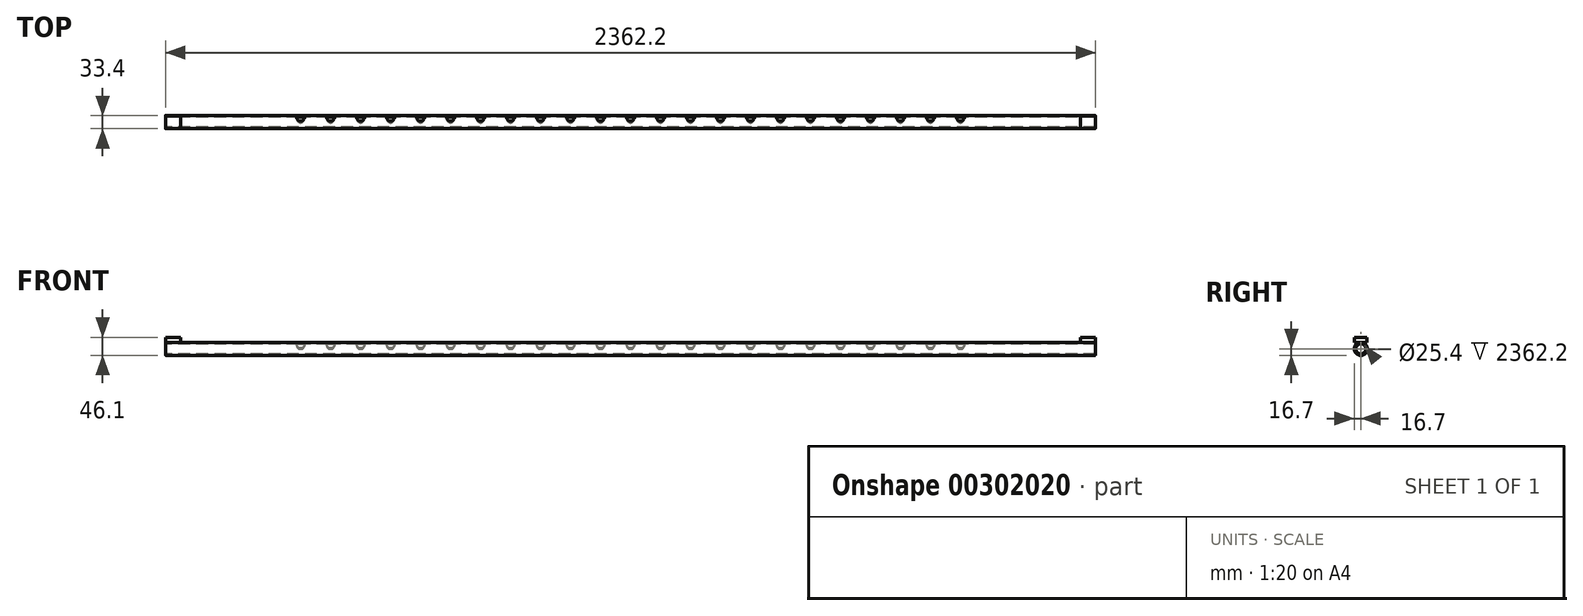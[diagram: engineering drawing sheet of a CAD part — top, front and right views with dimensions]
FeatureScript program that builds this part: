
annotation { "Feature Type Name" : "Feature", "Feature Type Description" : "" }
export const myFeature = defineFeature(function(context is Context, id is Id, definition is map)
    precondition{}
    {
        {
            var Q0;
            Q0=qCreatedBy(makeId("Right.planeOp"),FACE);
            var sketch = newSketch(context, id + "F0", { "sketchPlane" : qUnion([Q0])});
            skCircle(sketch, "E0", {"center": v(0, 0) * mm, "radius": 16.7 * mm});
            skCircle(sketch, "E1", {"center": v(0, 0) * mm, "radius": 12.7 * mm});
            skSolve(sketch);
        }
        {
            var Q0;
            Q0=qSketchRegion(id+"F0",true);
            extrude(context, id + "F1", {"entities" : qUnion([Q0]), "endBound" : BoundingType.SYMMETRIC, "depth" : 2362.2 * mm});
        }
        {
            var Q0;
            Q0=qCreatedBy(makeId("Top.planeOp"),FACE);
            cPlane(context, id + "F2", {"entities" : qUnion([Q0]), "cplaneType" : CPlaneType.OFFSET, "offset" : 16.7 * mm, "width" : 152.4 * mm, "height" : 152.4 * mm});
        }
        {
            var Q0;
            Q0=qCreatedBy(id+"F2.planeOp",FACE);
            var sketch = newSketch(context, id + "F3", { "sketchPlane" : qUnion([Q0])});
            skLineSegment(sketch, "E2", {"start": v(0, 113.47) * mm, "end": v(0, -135.26) * mm, "construction": true});
            skLineSegment(sketch, "E3", {"start": v(-1283.9, 0) * mm, "end": v(1277.96, 0) * mm, "construction": true});
            skPoint(sketch, "E4", {"position": v(0, 0) * mm});
            skPoint(sketch, "E5.1.0.0", {"position": v(76.2, 0) * mm});
            skPoint(sketch, "E5.2.0.0", {"position": v(152.4, 0) * mm});
            skPoint(sketch, "E5.3.0.0", {"position": v(228.6, 0) * mm});
            skPoint(sketch, "E5.4.0.0", {"position": v(304.8, 0) * mm});
            skPoint(sketch, "E5.5.0.0", {"position": v(381, 0) * mm});
            skPoint(sketch, "E5.6.0.0", {"position": v(457.2, 0) * mm});
            skPoint(sketch, "E5.7.0.0", {"position": v(533.4, 0) * mm});
            skPoint(sketch, "E5.8.0.0", {"position": v(609.6, 0) * mm});
            skPoint(sketch, "E5.9.0.0", {"position": v(685.8, 0) * mm});
            skLineSegment(sketch, "E5.direction1", {"start": v(0, 0) * mm, "end": v(76.2, 0) * mm, "construction": true});
            skLineSegment(sketch, "E6.0", {"start": v(965.2, 113.47) * mm, "end": v(965.2, -135.26) * mm, "construction": true});
            skPoint(sketch, "E7.0.10.0", {"position": v(762, 0) * mm});
            skPoint(sketch, "E7.0.11.0", {"position": v(838.2, 0) * mm});
            skPoint(sketch, "E8.1.0.0", {"position": v(-76.2, 0) * mm});
            skPoint(sketch, "E8.2.0.0", {"position": v(-152.4, 0) * mm});
            skPoint(sketch, "E8.3.0.0", {"position": v(-228.6, 0) * mm});
            skPoint(sketch, "E8.4.0.0", {"position": v(-304.8, 0) * mm});
            skPoint(sketch, "E8.5.0.0", {"position": v(-381, 0) * mm});
            skPoint(sketch, "E8.6.0.0", {"position": v(-457.2, 0) * mm});
            skPoint(sketch, "E8.7.0.0", {"position": v(-533.4, 0) * mm});
            skPoint(sketch, "E8.8.0.0", {"position": v(-609.6, 0) * mm});
            skPoint(sketch, "E8.9.0.0", {"position": v(-685.8, 0) * mm});
            skPoint(sketch, "E8.10.0.0", {"position": v(-762, 0) * mm});
            skPoint(sketch, "E8.11.0.0", {"position": v(-838.2, 0) * mm});
            skLineSegment(sketch, "E8.direction1", {"start": v(0, 0) * mm, "end": v(-76.2, 0) * mm, "construction": true});
            skSolve(sketch);
        }
        {
            var Q0;
            Q0=sQuery(id+"F3.wireOp",VERTEX,"E8.11.0.0");
            var Q1;
            Q1=sQuery(id+"F3.wireOp",VERTEX,"E8.10.0.0");
            var Q2;
            Q2=sQuery(id+"F3.wireOp",VERTEX,"E8.9.0.0");
            var Q3;
            Q3=sQuery(id+"F3.wireOp",VERTEX,"E8.8.0.0");
            var Q4;
            Q4=sQuery(id+"F3.wireOp",VERTEX,"E8.7.0.0");
            var Q5;
            Q5=sQuery(id+"F3.wireOp",VERTEX,"E8.6.0.0");
            var Q6;
            Q6=sQuery(id+"F3.wireOp",VERTEX,"E8.5.0.0");
            var Q7;
            Q7=sQuery(id+"F3.wireOp",VERTEX,"E8.4.0.0");
            var Q8;
            Q8=sQuery(id+"F3.wireOp",VERTEX,"E8.3.0.0");
            var Q9;
            Q9=sQuery(id+"F3.wireOp",VERTEX,"E8.2.0.0");
            var Q10;
            Q10=sQuery(id+"F3.wireOp",VERTEX,"E8.1.0.0");
            var Q11;
            Q11=sQuery(id+"F3.wireOp",VERTEX,"E4");
            var Q12;
            Q12=sQuery(id+"F3.wireOp",VERTEX,"E5.1.0.0");
            var Q13;
            Q13=sQuery(id+"F3.wireOp",VERTEX,"E5.2.0.0");
            var Q14;
            Q14=sQuery(id+"F3.wireOp",VERTEX,"E5.3.0.0");
            var Q15;
            Q15=sQuery(id+"F3.wireOp",VERTEX,"E5.4.0.0");
            var Q16;
            Q16=sQuery(id+"F3.wireOp",VERTEX,"E5.5.0.0");
            var Q17;
            Q17=sQuery(id+"F3.wireOp",VERTEX,"E5.6.0.0");
            var Q18;
            Q18=sQuery(id+"F3.wireOp",VERTEX,"E5.7.0.0");
            var Q19;
            Q19=sQuery(id+"F3.wireOp",VERTEX,"E5.8.0.0");
            var Q20;
            Q20=sQuery(id+"F3.wireOp",VERTEX,"E5.9.0.0");
            var Q21;
            Q21=sQuery(id+"F3.wireOp",VERTEX,"E7.0.10.0");
            var Q22;
            Q22=sQuery(id+"F3.wireOp",VERTEX,"E7.0.11.0");
            var Q23;
            Q23=makeQuery(id+"F1.opExtrude","SWEPT_BODY",BODY,{"disambiguationData":[OSD([sQuery(id+"F0.wireOp",EDGE,"E0"),sQuery(id+"F0.wireOp",EDGE,"E1")])]});
            hole(context, id + "F4", {"style" : HoleStyle.SIMPLE, "endStyle" : HoleEndStyle.BLIND, "holeDiameter" : 20.57 * mm, "holeDepth" : 12.7 * mm, "tappedDepth" : 24.13 * mm, "tapClearance" : 3, "startFromSketch" : true, "locations" : qUnion([Q0, Q1, Q2, Q3, Q4, Q5, Q6, Q7, Q8, Q9, Q10, Q11, Q12, Q13, Q14, Q15, Q16, Q17, Q18, Q19, Q20, Q21, Q22]), "scope" : qUnion([Q23])});
        }
        {
            var Q0;
            Q0=qCreatedBy(makeId("Top.planeOp"),FACE);
            var sketch = newSketch(context, id + "F5", { "sketchPlane" : qUnion([Q0])});
            skLineSegment(sketch, "E9", {"start": v(-1480.6, 0) * mm, "end": v(1384.83, 0) * mm, "construction": true});
            skSolve(sketch);
        }
        {
            var Q0;
            Q0=makeQuery(id+"F1.opExtrude","SWEPT_BODY",BODY,{"disambiguationData":[OSD([sQuery(id+"F0.wireOp",EDGE,"E0"),sQuery(id+"F0.wireOp",EDGE,"E1")])]});
            var Q1;
            Q1=sQuery(id+"F5.wireOp",EDGE,"E9");
            transform(context, id + "F6", {"entities" : qUnion([Q0]), "transformType" : TransformType.ROTATION, "transformAxis" : qUnion([Q1]), "angle" : 135 * degree, "makeCopy" : false});
        }
        {
            var Q0;
            Q0=makeQuery(id+"F1.opExtrude","CAP_FACE",FACE,{"disambiguationData":[OSD([sQuery(id+"F0.wireOp",EDGE,"E0"),sQuery(id+"F0.wireOp",EDGE,"E1")])],"isStart":false});
            var sketch = newSketch(context, id + "F7", { "sketchPlane" : qUnion([Q0])});
            skLineSegment(sketch, "E10", {"start": v(0, 0) * mm, "end": v(0, 32.37) * mm, "construction": true});
            skLineSegment(sketch, "E11.0", {"start": v(15.88, 0) * mm, "end": v(15.88, 32.37) * mm, "construction": true});
            skLineSegment(sketch, "E12", {"start": v(-61.16, 0) * mm, "end": v(62.55, 0) * mm, "construction": true});
            skLineSegment(sketch, "E13.0", {"start": v(-61.16, 16.7) * mm, "end": v(62.55, 16.7) * mm, "construction": true});
            skLineSegment(sketch, "E14.bottom", {"start": v(15.88, 16.7) * mm, "end": v(-15.88, 16.7) * mm});
            skLineSegment(sketch, "E14.top", {"start": v(15.88, 29.4) * mm, "end": v(-15.88, 29.4) * mm});
            skLineSegment(sketch, "E14.left", {"start": v(15.88, 16.7) * mm, "end": v(15.88, 29.4) * mm});
            skLineSegment(sketch, "E14.right", {"start": v(-15.88, 16.7) * mm, "end": v(-15.88, 29.4) * mm});
            skSolve(sketch);
        }
        {
            var Q0;
            Q0=qSketchRegion(id+"F7",true);
            extrude(context, id + "F8", {"entities" : qUnion([Q0]), "oppositeDirection" : true, "depth" : 38.1 * mm});
        }
        {
            var Q0;
            Q0=makeQuery(id+"F8.opExtrude","SWEPT_BODY",BODY,{"disambiguationData":[OSD([sQuery(id+"F7.wireOp",EDGE,"E14.bottom"),sQuery(id+"F7.wireOp",EDGE,"E14.top"),sQuery(id+"F7.wireOp",EDGE,"E14.left"),sQuery(id+"F7.wireOp",EDGE,"E14.right")])]});
            var Q1;
            Q1=qCreatedBy(makeId("Right.planeOp"),FACE);
            mirror(context, id + "F9", {"entities" : qUnion([Q0]), "mirrorPlane" : qUnion([Q1])});
        }
        {
            var Q0;
            Q0=makeQuery(id+"F1.opExtrude","SWEPT_BODY",BODY,{"disambiguationData":[OSD([sQuery(id+"F0.wireOp",EDGE,"E0"),sQuery(id+"F0.wireOp",EDGE,"E1")])]});
            var Q1;
            Q1=sQuery(id+"F5.wireOp",EDGE,"E9");
            transform(context, id + "F10", {"entities" : qUnion([Q0]), "transformType" : TransformType.ROTATION, "transformAxis" : qUnion([Q1]), "angle" : 180 * degree, "makeCopy" : false});
        }
    });
